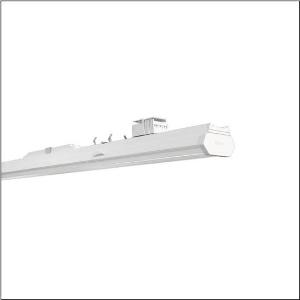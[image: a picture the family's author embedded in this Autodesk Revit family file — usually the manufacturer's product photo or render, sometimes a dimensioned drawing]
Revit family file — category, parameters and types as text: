
# Revit family: licross_r__21_protected_mo_52tp12cn49xg_2097
name_source: partatom
category: Lighting Fixtures
units: mm (PartAtom-declared; Revit-internal decimal feet)

## family parameters
Cut with Voids When Loaded = No
Host = Face
Light Source = No
Part Type = Normal
Room Calculation Point = No
Round Connector Dimension = Use Diameter
Shared = No

## types (1)
- --- (1 x LED, 9110 lm, 50.4 W, 4000K)
    Apparent Load = 50 VA
    CIE Flux Codes = 73 92 98 99 100
    Color Rendering = 80
    Color Temperature = 4000K
    Default Elevation = 1800 mm
    Description = Licross® 21 Protected MO, luminaire insert, of sheet steel, galvanised, coil coated, white, length: 1.500mm, width: 90mm, height: 103mm, LED rated luminous flux: 9.120lm, light colour: 840, control gear: ON/OFF Multilumen, CLOi, control gear: ECG Multilumen, with plug, 3-pole, with phase selection, mains connection: 220..240V, AC, 50/60Hz, start of lifetime: 50W, end of service life: 61W, halogen-free wiring, primary light control with lens, of plastic, primary optical cover: cover, of PMMA, light emission: direct distribution, primary light characteristic: symmetric, protection rating (complete): IP64, insulation class (complete): insulation class I (protective earthing), certification: CE, ENEC, VDE, UKCA, protection symbol: D if used in an environment with conductive dust loads with corresponding accessories, impact resistance: IK06, permissible ambient temperature for indoor applications: -35..+45°C, corresponds to IFS (International Featured Standards) requirements for safety and quality in the food industry, reducing of maximum allowable ambient temperature of 5°C with ceiling mounting, LABS conformity tested according to VDMA 24364:2018-05, packaging unit: 1 piece
    Height = 92 mm
    Lamp = 1 x LED
    Lamp Light Flux = 9110 lm
    Lamp Power = 50.4 W
    Lamp count = 1
    Length = 1500 mm
    Luminous efficacy = 181 lm/W
    Manufacturer = Siteco
    ModVariant = No
    Model = 52TP12CN49XG
    Mounting Place = Ceiling
    Mounting Type = Pendant
    Number of Poles = 1
    OnlyDefault = Yes
    Power Factor = 1
    Product Name = Licross® 21 Protected MO
    Product group = luminaire insert
    ProductGroupID = 901
    Protection Class = Protection class I
    Protection Degree = IP 64
    RLX_Detail_Level = 1
    RLX_Emergency_Light_Flux = 0 lm
    RLX_Emergency_Type = 0
    RLX_Emergency_Type_DB = No
    RlxData = <blob elided: 22265 chars, md5=ef04878e>
    Socket = socket
    Standby Power = 0 W
    System Light Flux = 9110 lm
    System Power = 50 W
    Type Comments = factory setting: luminous flux: 100 % | (A | C | E) | 117 mA
    Type Image = l_1256148.jpg
    URL = http://relux.com
    VarID = @adj_080037
    Voltage = 0 V
    Weight = 0.00 kg
    Width = 88 mm

## geometry (parser evidence)
native form markers: Blend x4, Sweep x11
no freeform markers — native parametric forms only
